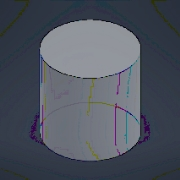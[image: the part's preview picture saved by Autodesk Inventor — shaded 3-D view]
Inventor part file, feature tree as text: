
AUTODESK INVENTOR PART (.ipt)
format: ipt  version: 2024.3 (Build 283343000, 343)  size: 134,656 bytes
history: native  units: mm
features: extrude x1, sketch x1
ambient origin geometry x8: Origin, YZ Plane, XZ Plane, XY Plane, X Axis, Y Axis, Z Axis, Center Point
bodies: Solid1 (feature_tree)
feature tree (2):
  extrude  "Extrusion1"  [1 undecoded]
  sketch  "Sketch1"  dims[d1=70.0mm d2=0.0mm]
note: 1 required parameter value undecoded (feature->parameter linkage not recoverable at this tier; creation-order binding heuristic only, values carry confidence <= 0.55)
